# Revit family: 330_8a6c91d07f81446b859301ba4aecb0
name_source: partatom
category: Mechanical Equipment
units: mm (PartAtom-declared; Revit-internal decimal feet)

## family parameters
Always vertical = Yes
Classification = None
Cut with Voids When Loaded = No
Maintain Annotation Orientation = No
Part Type = Normal
Room Calculation Point = No
Round Connector Dimension = Use Diameter
Shared = No
Work Plane-Based = No

## types (1)
- 2171 1180EA
    CAT = No
    CAT0 = Yes
    CenSd_R13_6 = 18 mm
    CenSd_R15_6 = 15 mm  [stored 0.0492126 ft]
    CenSd_R1_6 = 11 mm
    CenSd_R25_6 = 22 mm
    Default Elevation = 0 mm  [stored 0 ft]
    Description = Booster unit, high eff. pump 1-8 m, shut-off valves, 180 mm
    H = 434 mm  [stored 1.42388 ft]
    H2 = 217 mm  [stored 0.711942 ft]
    KH = 15 mm  [stored 0.0492126 ft]
    L = 245 mm
    L10 = 10 mm  [stored 0.0328084 ft]
    L10__ve = -10 mm  [stored -0.0328084 ft]
    L15 = 16 mm  [stored 0.0524934 ft]
    L2 = 123 mm
    L20 = 20 mm  [stored 0.0656168 ft]
    L20__ve = -20 mm  [stored -0.0656168 ft]
    L22 = 5 mm  [stored 0.0164042 ft]
    L222 = 2 mm  [stored 0.00656168 ft]
    L222__ve = -2 mm  [stored -0.00656168 ft]
    L22__ve = -5 mm  [stored -0.0164042 ft]
    L30 = 32 mm  [stored 0.104987 ft]
    L45 = 45 mm  [stored 0.147638 ft]
    L5 = 5 mm  [stored 0.0164042 ft]
    LH4 = 132 mm
    LH42 = 66 mm
    LH44 = 112 mm
    LH48 = 142 mm
    LH6 = 62 mm  [stored 0.203412 ft]
    LH61 = 94 mm  [stored 0.308399 ft]
    LH62 = 31 mm
    LH9 = 48 mm
    LH92 = 24 mm
    MC Product Code = 2171 1180EA
    MC Shunt Control Valve Location = 0
    MC Shunt Valve Configuration = 0
    Manufacturer = FAR
    P1 = 25 mm
    P2 = 25 mm
    PL = 49 mm
    QmdConnectorList = 301;P2;302;P2;303;P1;304;P1
    R1 = 13 mm
    R13 = 21 mm
    R15 = 18 mm
    R2 = 13 mm
    R25 = 26 mm
    W = 170 mm
    W2 = 85 mm
    W2L = 80 mm  [stored 0.262467 ft]
    W2L__ve = -80 mm  [stored -0.262467 ft]
    WL = 225 mm  [stored 0.738189 ft]
    XC = 63 mm
    magiPartTypeId = 330
    magiProductFamilyId = 8a6c91d07f81446b859301ba4aecb0
    magiProductId = 8a6c91d07f81446b859301ba4aecb0

note: [stored X ft] marks values corroborated as IEEE doubles in the binary element streams (Revit-internal decimal feet)

## geometry (parser evidence)
native form markers: Sweep x3
no freeform markers — native parametric forms only
